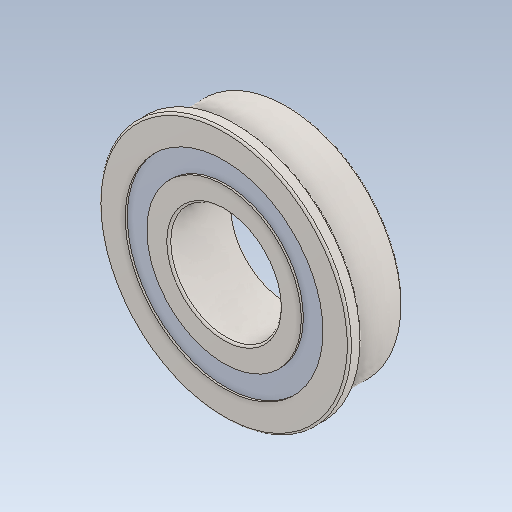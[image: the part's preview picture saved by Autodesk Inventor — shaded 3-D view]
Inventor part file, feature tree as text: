
AUTODESK INVENTOR PART (.ipt)
format: ipt  version: 2020 (Build 240168000, 168)  size: 208,384 bytes
history: native  units: in
note: dims shown in document units (in); Inventor stores cm internally (conversion verified against a paired STEP export)
features: fillet x1
ambient origin geometry x8: Origin, YZ Plane, XZ Plane, XY Plane, X Axis, Y Axis, Z Axis, Center Point
bodies: Solid1 (feature_tree)
feature tree (1):
  fillet  "Fillet1"  [1 undecoded]
note: 1 required parameter value undecoded (feature->parameter linkage not recoverable at this tier; creation-order binding heuristic only, values carry confidence <= 0.55)
